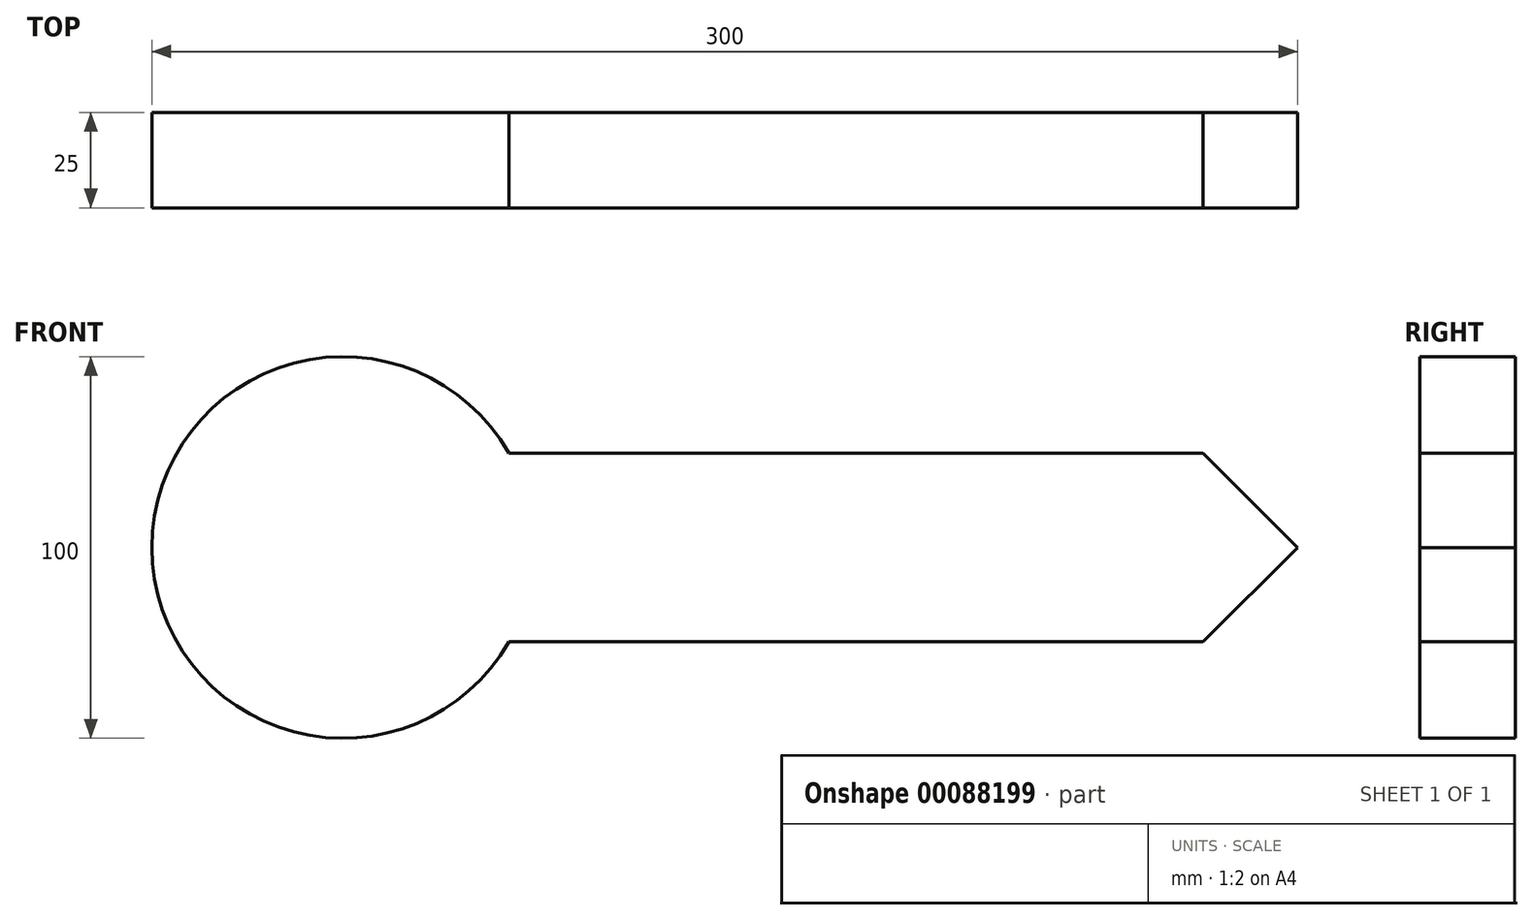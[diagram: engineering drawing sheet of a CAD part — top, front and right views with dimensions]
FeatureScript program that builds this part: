
annotation { "Feature Type Name" : "Feature", "Feature Type Description" : "" }
export const myFeature = defineFeature(function(context is Context, id is Id, definition is map)
    precondition{}
    {
        {
            var Q0;
            Q0=qCreatedBy(makeId("Front.planeOp"),FACE);
            var sketch = newSketch(context, id + "F0", { "sketchPlane" : qUnion([Q0])});
            skArc(sketch, "E0", {"start": v(43.45, 24.75) * mm, "mid": v(-50, 0) * mm, "end": v(43.45, -24.75) * mm});
            skLineSegment(sketch, "E1", {"start": v(0, 0) * mm, "end": v(250, 0) * mm, "construction": true});
            skLineSegment(sketch, "E2", {"start": v(250, 0) * mm, "end": v(225.25, 24.75) * mm});
            skLineSegment(sketch, "E3", {"start": v(225.25, 24.75) * mm, "end": v(43.45, 24.75) * mm});
            skLineSegment(sketch, "E4.MirrorCS", {"start": v(250, 0) * mm, "end": v(225.25, -24.75) * mm});
            skLineSegment(sketch, "E5.MirrorCS", {"start": v(225.25, -24.75) * mm, "end": v(43.45, -24.75) * mm});
            skSolve(sketch);
        }
        {
            var Q0;
            Q0=sQuery(id+"F0.wireOp",EDGE,"E4.MirrorCS");
            var Q1;
            Q1=sQuery(id+"F0.wireOp",EDGE,"E5.MirrorCS");
            var Q2;
            Q2=sQuery(id+"F0.wireOp",EDGE,"E3");
            var Q3;
            Q3=sQuery(id+"F0.wireOp",EDGE,"E2");
            var Q4;
            Q4=sQuery(id+"F0.wireOp",EDGE,"E0");
            extrude(context, id + "F1", {"bodyType" : ToolBodyType.SURFACE, "surfaceEntities" : qUnion([Q0, Q1, Q2, Q3, Q4]), "depth" : 25 * mm});
        }
    });
